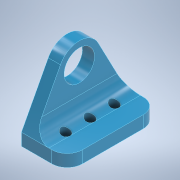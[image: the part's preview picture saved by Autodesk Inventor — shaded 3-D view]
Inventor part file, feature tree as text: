
AUTODESK INVENTOR PART (.ipt)
format: ipt  version: 2021 (Build 250183000, 183)  size: 240,640 bytes
history: native  units: mm
features: extrude x5, sketch x3, other x3, revolve x2, fillet x2
ambient origin geometry x8: Origin, YZ Plane, XZ Plane, XY Plane, X Axis, Y Axis, Z Axis, Center Point
bodies: Body (feature_tree)
feature tree (15):
  sketch  "Sketch1"  dims[d0=6.0mm d1=5.0mm]
  revolve  "Revolution1"  [1 undecoded]
  revolve  "Revolution2"  [1 undecoded]
  extrude  "Extrusion1"  Depth=5.0mm
  extrude  "Extrusion2"  Depth=4.125mm
  sketch  "Sketch2"  dims[d2=1.5mm d3=0.25mm]
  extrude  "Extrusion3"  Depth=4.0mm
  extrude  "Extrusion4"  Depth=5.0mm
  sketch  "Sketch3"  dims[d5=2.75mm d6=5.0mm d7=4.125mm d8=4.0mm d9=3.8mm d10=6.75mm d11=4.0mm d12=2.0mm d13=5.0mm d14=11.0mm d15=4.125mm d16=90.0deg d17=90.0deg d18=0.0mm d19=0.0mm d20=8.25mm d21=0.0mm d22=10.0mm d23=4.0mm d24=2.0mm d25=17.5mm d26=30.0mm d27=4.0mm d28=0.0mm d29=15.0mm d30=0.0mm d31=5.0mm d32=3.0mm d33=3.0mm d34=3.0mm d35=16.0mm d36=7.5mm d37=30.0mm d38=0.0mm d39=5.0mm]
  fillet  "Fillet1"  Radius=6.75mm
  extrude  "Extrusion5"  Depth=4.0mm
  fillet  "Fillet2"  Radius=2.0mm
  other  "Lens"
  other  "PCB"
  other  "Mount"
note: 2 required parameter values undecoded (feature->parameter linkage not recoverable at this tier; creation-order binding heuristic only, values carry confidence <= 0.55)
